# Revit family: Toilet_Wall-Mnt
name_source: partatom
category: Plumbing Fixtures
units: mm (PartAtom-declared; Revit-internal decimal feet)

## family parameters
Always vertical = Yes
Classification Number = 23.45.05.21.11
Cut with Voids When Loaded = No
Enable Cutting in Views = No
Maintain Annotation Orientation = No
Part Type = Normal
Room Calculation Point = No
Round Connector Dimension = Use Diameter
Shared = No
Work Plane-Based = Yes

## types (2) — shared parameters
Assembly Code = D2010110
CW Connection = Yes
CWFU = 0.25
Connection = 1/2" NPT
Construction Details = http://www.arcat.com
Default Elevation = 4' - 0"
Description = 2 Piece Toilet - Elongated
Expected Lifespan (Years) = 20
Flush = Pressure Valve - Automatic
GPF = 1.6
Green Building-LEED = http://www.arcat.com
HW Connection = No
Keynote = 15410
Maintenance Schedule (Months) = 60
Manufacturer = Generic
Manufacturer Fax = (203) 939-2444
Manufacturer Website = http://www.arcat.com
Material - Bath Fittings = ARCAT - Ceramic - Porcelain
Material - Bath Fixture Accent = ARCAT - Plastic - White
Material - Bath Fixtures = ARCAT - Metal - Steel
Model = Generic
Product Data = http://www.arcat.com
Product Properties = http://www.arcat.com
Specification = http://www.arcat.com
Vent Connection = No
WFU = 1.6
Warranty Duration (Years) = 10
Waste Connection = Yes

## type names (no varying parameters)
- White
- Black

## geometry (parser evidence)
native form markers: Sweep x5
no freeform markers — native parametric forms only
